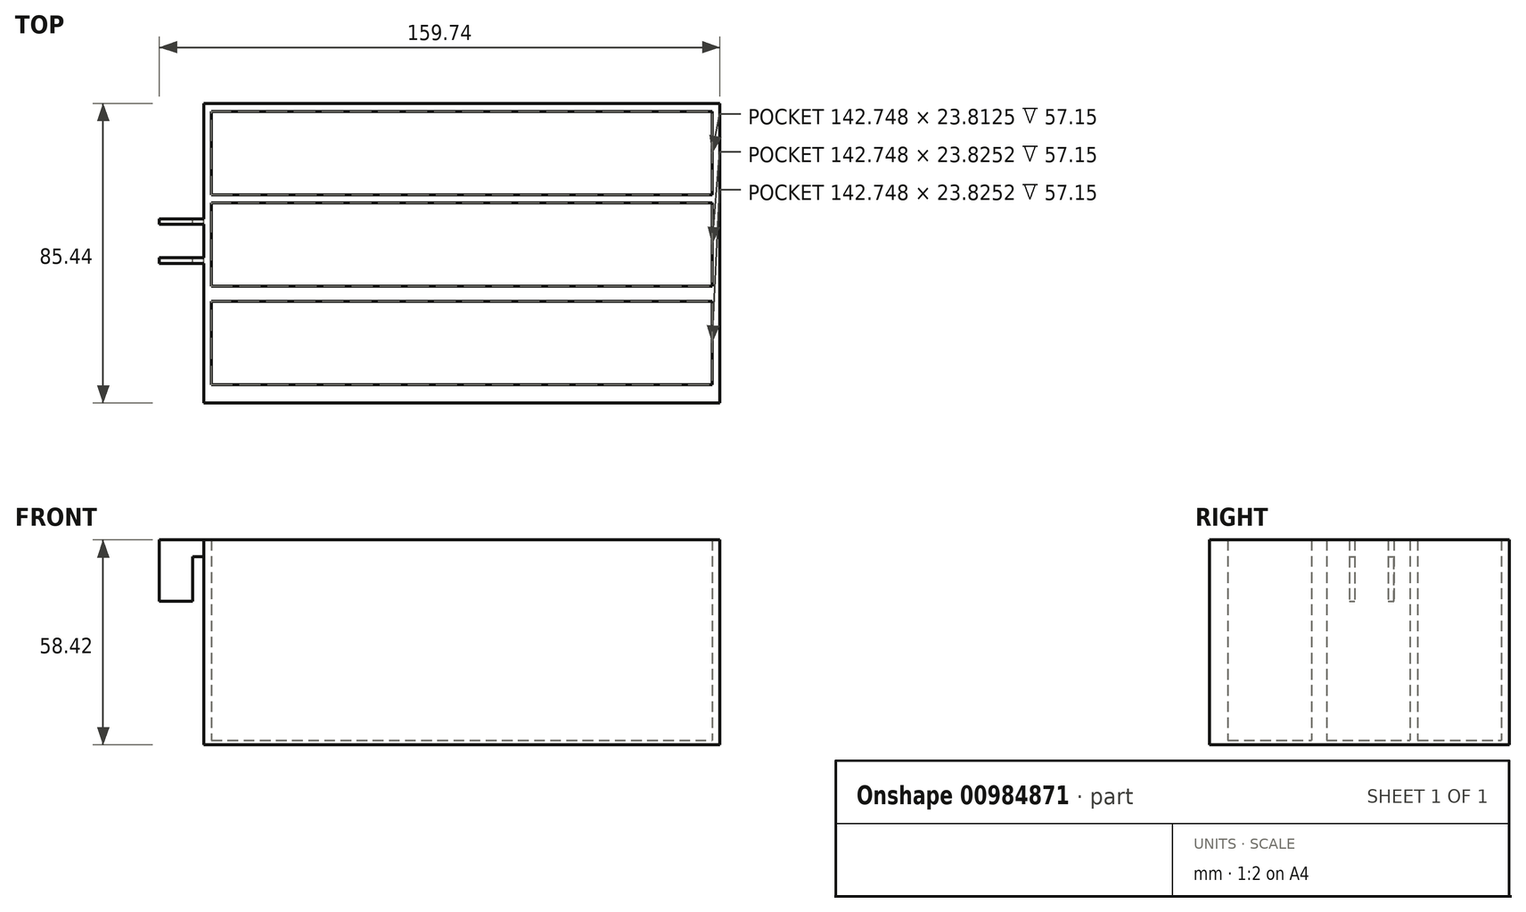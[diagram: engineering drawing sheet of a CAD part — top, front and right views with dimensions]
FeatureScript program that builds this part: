
annotation { "Feature Type Name" : "Feature", "Feature Type Description" : "" }
export const myFeature = defineFeature(function(context is Context, id is Id, definition is map)
    precondition{}
    {
        {
            var Q0;
            Q0=qCreatedBy(makeId("Top.planeOp"),FACE);
            var sketch = newSketch(context, id + "F0", { "sketchPlane" : qUnion([Q0])});
            skLineSegment(sketch, "E0.bottom", {"start": v(71.37, -40.39) * mm, "end": v(-71.37, -40.39) * mm});
            skLineSegment(sketch, "E0.top", {"start": v(71.37, 40.39) * mm, "end": v(-71.37, 40.39) * mm});
            skLineSegment(sketch, "E0.left", {"start": v(71.37, -40.39) * mm, "end": v(71.37, 40.39) * mm});
            skLineSegment(sketch, "E0.right", {"start": v(-71.37, -40.39) * mm, "end": v(-71.37, 40.39) * mm});
            skPoint(sketch, "E0.middle", {"position": v(0, 0) * mm});
            skLineSegment(sketch, "E1.bottom", {"start": v(73.52, -42.72) * mm, "end": v(-73.52, -42.72) * mm});
            skLineSegment(sketch, "E1.top", {"start": v(73.52, 42.72) * mm, "end": v(-73.52, 42.72) * mm});
            skLineSegment(sketch, "E1.left", {"start": v(73.52, -42.72) * mm, "end": v(73.52, 42.72) * mm});
            skLineSegment(sketch, "E1.right", {"start": v(-73.52, -42.72) * mm, "end": v(-73.52, 42.72) * mm});
            skLineSegment(sketch, "E2.bottom", {"start": v(-71.37, 40.39) * mm, "end": v(71.37, 40.39) * mm});
            skLineSegment(sketch, "E2.top", {"start": v(-71.37, 16.57) * mm, "end": v(71.37, 16.57) * mm});
            skLineSegment(sketch, "E2.left", {"start": v(-71.37, 40.39) * mm, "end": v(-71.37, 16.57) * mm});
            skLineSegment(sketch, "E2.right", {"start": v(71.37, 40.39) * mm, "end": v(71.37, 16.57) * mm});
            skLineSegment(sketch, "E3.bottom", {"start": v(-71.37, 14.4) * mm, "end": v(71.37, 14.4) * mm});
            skLineSegment(sketch, "E3.top", {"start": v(-71.37, -9.42) * mm, "end": v(71.37, -9.42) * mm});
            skLineSegment(sketch, "E3.left", {"start": v(-71.37, 14.4) * mm, "end": v(-71.37, -9.42) * mm});
            skLineSegment(sketch, "E3.right", {"start": v(71.37, 14.4) * mm, "end": v(71.37, -9.42) * mm});
            skLineSegment(sketch, "E4.bottom", {"start": v(-71.37, -13.68) * mm, "end": v(71.37, -13.68) * mm});
            skLineSegment(sketch, "E4.top", {"start": v(-71.37, -37.5) * mm, "end": v(71.37, -37.5) * mm});
            skLineSegment(sketch, "E4.left", {"start": v(-71.37, -13.68) * mm, "end": v(-71.37, -37.5) * mm});
            skLineSegment(sketch, "E4.right", {"start": v(71.37, -13.68) * mm, "end": v(71.37, -37.5) * mm});
            skSolve(sketch);
        }
        {
            var Q0;
            {var subQ13=sQuery(id+"F0.wireOp",EDGE,"E0.bottom");Q0=makeQuery(id+"F0.imprint","IMPRINT",FACE,{"disambiguationData":[TD([[makeQuery(id+"F0.imprint","IMPRINT",EDGE,{"derivedFrom":subQ13}),1.0]])]});}
            var Q1;
            {var subQ0=sQuery(id+"F0.wireOp",EDGE,"E2.top");Q1=makeQuery(id+"F0.imprint","IMPRINT",FACE,{"disambiguationData":[TD([[makeQuery(id+"F0.imprint","IMPRINT",EDGE,{"derivedFrom":subQ0}),-1.0]])]});}
            var Q2;
            {var subQ0=sQuery(id+"F0.wireOp",EDGE,"E3.top");Q2=makeQuery(id+"F0.imprint","IMPRINT",FACE,{"disambiguationData":[TD([[makeQuery(id+"F0.imprint","IMPRINT",EDGE,{"derivedFrom":subQ0}),-1.0]])]});}
            var Q3;
            {var subQ0=sQuery(id+"F0.wireOp",EDGE,"E0.bottom");Q3=makeQuery(id+"F0.imprint","IMPRINT",FACE,{"disambiguationData":[TD([[makeQuery(id+"F0.imprint","IMPRINT",EDGE,{"derivedFrom":subQ0}),-1.0]])]});}
            extrude(context, id + "F1", {"entities" : qUnion([Q0, Q1, Q2, Q3]), "depth" : 58.42 * mm, "offsetDistance" : 25.4 * mm});
        }
        {
            var Q0;
            {var subQ13=sQuery(id+"F0.wireOp",EDGE,"E0.bottom");Q0=makeQuery(id+"F0.imprint","IMPRINT",FACE,{"disambiguationData":[TD([[makeQuery(id+"F0.imprint","IMPRINT",EDGE,{"derivedFrom":subQ13}),1.0]])]});}
            var Q1;
            {var subQ0=sQuery(id+"F0.wireOp",EDGE,"E0.top");Q1=makeQuery(id+"F0.imprint","IMPRINT",FACE,{"disambiguationData":[TD([[makeQuery(id+"F0.imprint","IMPRINT",EDGE,{"derivedFrom":subQ0}),1.0]])]});}
            var Q2;
            {var subQ0=sQuery(id+"F0.wireOp",EDGE,"E3.bottom");Q2=makeQuery(id+"F0.imprint","IMPRINT",FACE,{"disambiguationData":[TD([[makeQuery(id+"F0.imprint","IMPRINT",EDGE,{"derivedFrom":subQ0}),-1.0]])]});}
            var Q3;
            {var subQ2=sQuery(id+"F0.wireOp",EDGE,"E4.bottom");Q3=makeQuery(id+"F0.imprint","IMPRINT",FACE,{"disambiguationData":[TD([[makeQuery(id+"F0.imprint","IMPRINT",EDGE,{"derivedFrom":subQ2}),-1.0]])]});}
            extrude(context, id + "F2", {"entities" : qUnion([Q0, Q1, Q2, Q3]), "operationType" : NewBodyOperationType.ADD, "depth" : 1.27 * mm, "offsetDistance" : 25.4 * mm});
        }
        {
            var Q0;
            Q0=makeQuery(id+"F1.opExtrude","SWEPT_FACE",FACE,{"disambiguationData":[OSD([sQuery(id+"F0.wireOp",EDGE,"E1.right")])]});
            var sketch = newSketch(context, id + "F3", { "sketchPlane" : qUnion([Q0])});
            skLineSegment(sketch, "E5.bottom", {"start": v(1.31, 58.42) * mm, "end": v(2.91, 58.42) * mm});
            skLineSegment(sketch, "E5.top", {"start": v(1.31, 40.94) * mm, "end": v(2.91, 40.94) * mm});
            skLineSegment(sketch, "E5.left", {"start": v(1.31, 58.42) * mm, "end": v(1.31, 40.94) * mm});
            skLineSegment(sketch, "E5.right", {"start": v(2.91, 58.42) * mm, "end": v(2.91, 40.94) * mm});
            skLineSegment(sketch, "E6.bottom", {"start": v(-8.21, 58.42) * mm, "end": v(-9.81, 58.42) * mm});
            skLineSegment(sketch, "E6.top", {"start": v(-8.21, 40.94) * mm, "end": v(-9.81, 40.94) * mm});
            skLineSegment(sketch, "E6.left", {"start": v(-8.21, 58.42) * mm, "end": v(-8.21, 40.94) * mm});
            skLineSegment(sketch, "E6.right", {"start": v(-9.81, 58.42) * mm, "end": v(-9.81, 40.94) * mm});
            skSolve(sketch);
        }
        {
            var Q0;
            Q0=makeQuery(id+"F3.imprint","IMPRINT",FACE,{"disambiguationData":[TD([[makeQuery(id+"F3.imprint","IMPRINT",EDGE,{"derivedFrom":sQuery(id+"F3.wireOp",EDGE,"E6.bottom")}),1.0]])]});
            var Q1;
            Q1=makeQuery(id+"F3.imprint","IMPRINT",FACE,{"disambiguationData":[TD([[makeQuery(id+"F3.imprint","IMPRINT",EDGE,{"derivedFrom":sQuery(id+"F3.wireOp",EDGE,"E5.bottom")}),1.0]])]});
            extrude(context, id + "F4", {"entities" : qUnion([Q0, Q1]), "operationType" : NewBodyOperationType.ADD, "depth" : 12.7 * mm, "offsetDistance" : 25.4 * mm});
        }
        {
            var Q0;
            Q0=makeQuery(id+"F4.opExtrude","SWEPT_FACE",FACE,{"disambiguationData":[OSD([sQuery(id+"F3.wireOp",EDGE,"E6.right")])]});
            var sketch = newSketch(context, id + "F5", { "sketchPlane" : qUnion([Q0])});
            skLineSegment(sketch, "E7.bottom", {"start": v(73.52, 40.94) * mm, "end": v(76.7, 40.94) * mm});
            skLineSegment(sketch, "E7.top", {"start": v(73.52, 53.64) * mm, "end": v(76.7, 53.64) * mm});
            skLineSegment(sketch, "E7.left", {"start": v(73.52, 40.94) * mm, "end": v(73.52, 53.64) * mm});
            skLineSegment(sketch, "E7.right", {"start": v(76.7, 40.94) * mm, "end": v(76.7, 53.64) * mm});
            skSolve(sketch);
        }
        {
            var Q0;
            Q0=makeQuery(id+"F5.imprint","IMPRINT",FACE,{"disambiguationData":[TD([[makeQuery(id+"F5.imprint","IMPRINT",EDGE,{"derivedFrom":sQuery(id+"F5.wireOp",EDGE,"E7.bottom")}),-1.0]])]});
            extrude(context, id + "F6", {"entities" : qUnion([Q0]), "operationType" : NewBodyOperationType.REMOVE, "oppositeDirection" : true, "depth" : 25.4 * mm, "offsetDistance" : 25.4 * mm});
        }
    });
